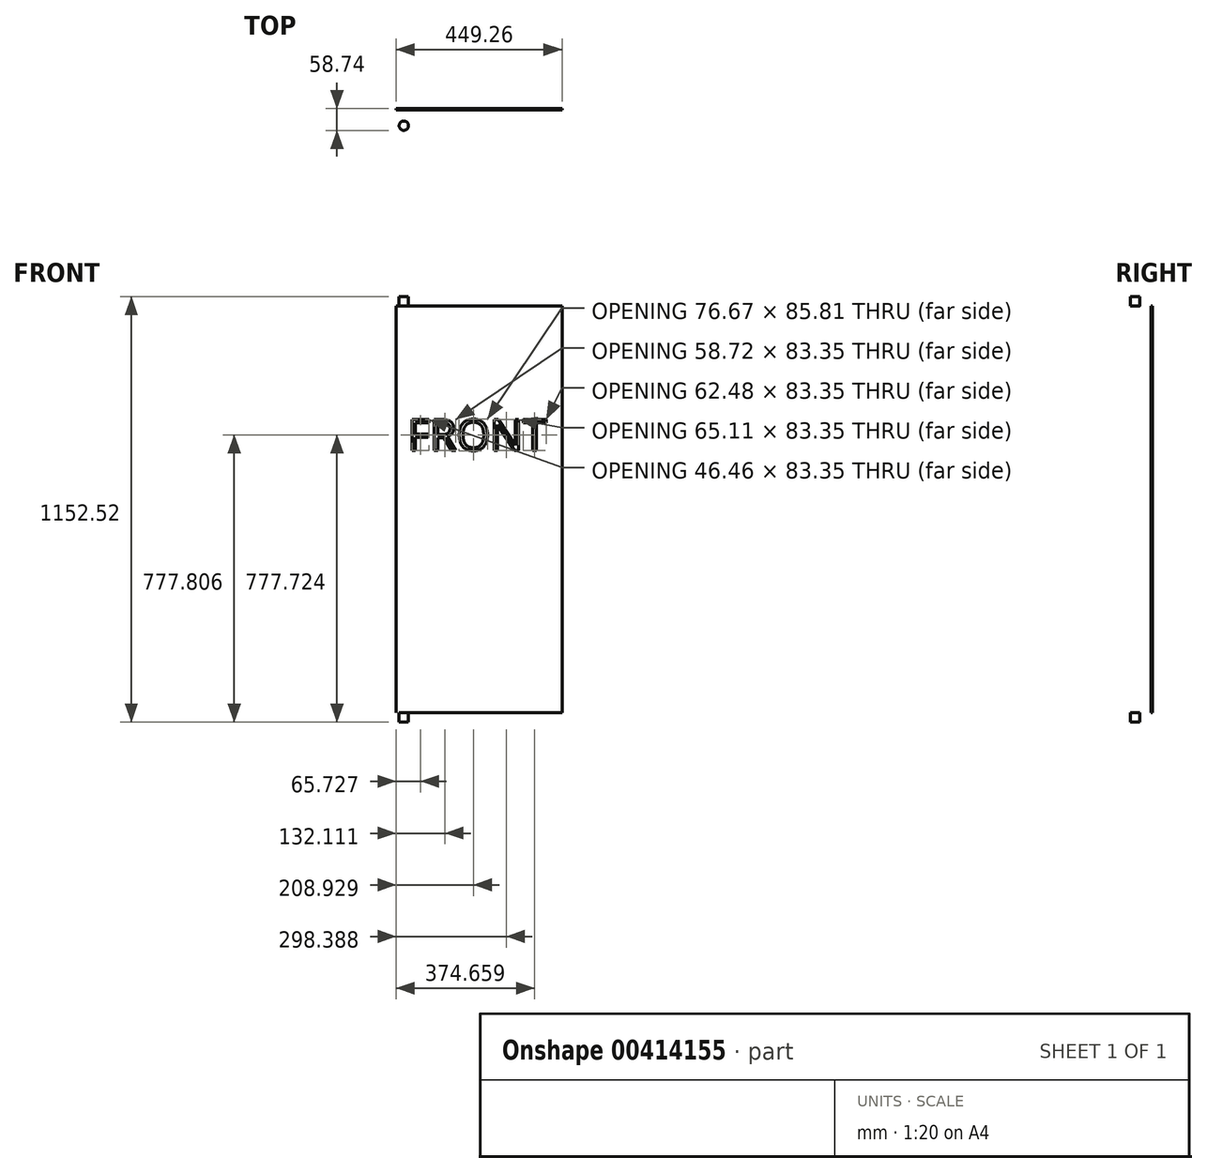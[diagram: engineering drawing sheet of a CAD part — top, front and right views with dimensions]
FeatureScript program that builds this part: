
annotation { "Feature Type Name" : "Feature", "Feature Type Description" : "" }
export const myFeature = defineFeature(function(context is Context, id is Id, definition is map)
    precondition{}
    {
        {
            var Q0;
            Q0=qCreatedBy(makeId("Front.planeOp"),FACE);
            var sketch = newSketch(context, id + "F0", { "sketchPlane" : qUnion([Q0])});
            skLineSegment(sketch, "E0.bottom", {"start": v(-217.6, 786.74) * mm, "end": v(231.66, 786.74) * mm});
            skLineSegment(sketch, "E0.top", {"start": v(-217.6, -314.98) * mm, "end": v(231.66, -314.98) * mm});
            skLineSegment(sketch, "E0.left", {"start": v(-217.6, 786.74) * mm, "end": v(-217.6, -314.98) * mm});
            skLineSegment(sketch, "E0.right", {"start": v(231.66, 786.74) * mm, "end": v(231.66, -314.98) * mm});
            skSolve(sketch);
        }
        {
            var Q0;
            Q0=makeQuery(id+"F0.imprint","IMPRINT",FACE,{"disambiguationData":[TD([[makeQuery(id+"F0.imprint","IMPRINT",EDGE,{"derivedFrom":sQuery(id+"F0.wireOp",EDGE,"E0.bottom")}),-1.0]])]});
            extrude(context, id + "F1", {"entities" : qUnion([Q0]), "depth" : (3 + (7 / 16)) * mm});
        }
        {
            var Q0;
            Q0=makeQuery(id+"F1.opExtrude","SWEPT_FACE",FACE,{"disambiguationData":[OSD([sQuery(id+"F0.wireOp",EDGE,"E0.bottom")])]});
            var sketch = newSketch(context, id + "F2", { "sketchPlane" : qUnion([Q0])});
            skCircle(sketch, "E1", {"center": v(-196.96, -46.04) * mm, "radius": 12.7 * mm});
            skSolve(sketch);
        }
        {
            var Q0;
            Q0 = qSketchRegion(id + "F2", true);
            extrude(context, id + "F3", {"entities" : qUnion([Q0]), "operationType" : NewBodyOperationType.ADD, "depth" : 25.4 * mm});
        }
        {
            var Q0;
            Q0=makeQuery(id+"F1.opExtrude","SWEPT_FACE",FACE,{"disambiguationData":[OSD([sQuery(id+"F0.wireOp",EDGE,"E0.top")])]});
            var sketch = newSketch(context, id + "F4", { "sketchPlane" : qUnion([Q0])});
            skCircle(sketch, "E2", {"center": v(-196.96, 46.04) * mm, "radius": 12.7 * mm});
            skSolve(sketch);
        }
        {
            var Q0;
            Q0 = qSketchRegion(id + "F4", true);
            extrude(context, id + "F5", {"entities" : qUnion([Q0]), "operationType" : NewBodyOperationType.ADD, "depth" : 25.4 * mm});
        }
        {
            var Q0;
            Q0=makeQuery(id+"F1.opExtrude","CAP_FACE",FACE,{"disambiguationData":[OSD([sQuery(id+"F0.wireOp",EDGE,"E0.bottom"),sQuery(id+"F0.wireOp",EDGE,"E0.top"),sQuery(id+"F0.wireOp",EDGE,"E0.left"),sQuery(id+"F0.wireOp",EDGE,"E0.right")])],"isStart":false});
            var sketch = newSketch(context, id + "F6", { "sketchPlane" : qUnion([Q0])});
            skText(sketch, "E3", { "text": "FRONT", "fontName": "OpenSans-Regular.ttf"});
            const initialGuessF6  = {"E3": [-0.18656, 0.39567, 1, 0, 0.08406]};
            skSetInitialGuess(sketch, initialGuessF6);
            skSolve(sketch);
        }
        {
            var Q0;
            Q0 = qSketchRegion(id + "F6", true);
            extrude(context, id + "F7", {"entities" : qUnion([Q0]), "operationType" : NewBodyOperationType.REMOVE, "oppositeDirection" : true, "depth" : 12.7 * mm});
        }
    });
